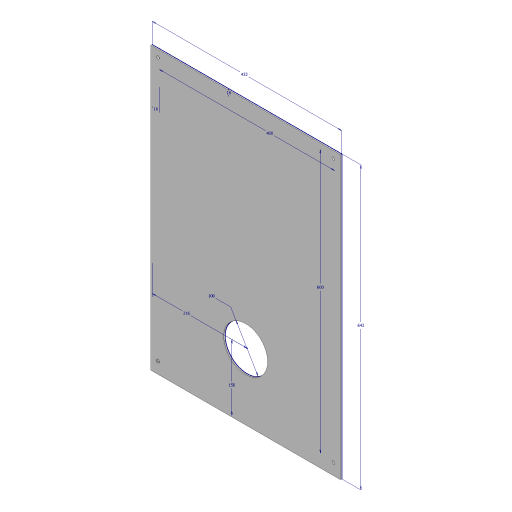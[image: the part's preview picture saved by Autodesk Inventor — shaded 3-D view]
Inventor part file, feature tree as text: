
AUTODESK INVENTOR PART (.ipt)
format: ipt  version: 2023 (Build 270158000, 158)  size: 101,376 bytes
history: native  units: mm
features: sketch x1, extrude x1, hole x1
ambient origin geometry x8: Origin, YZ Plane, XZ Plane, XY Plane, X Axis, Y Axis, Z Axis, Center Point
bodies: Solid1 (feature_tree)
feature tree (3):
  sketch  "Sketch1"  dims[d0=432.0mm d1=642.0mm d2=600.0mm d3=400.0mm d4=16.0mm d5=16.0mm d6=100.0mm d7=150.0mm d8=216.0mm d9=3.0mm d10=0.0mm d11=6.4mm d12=6.0mm d13=4.0mm d14=2.0mm d15=90.0deg d16=8.0mm d17=20.594885mm]
  extrude  "Extrusion1"  Depth=642.0mm
  hole  "Hole1"  [1 undecoded]
note: 1 required parameter value undecoded (feature->parameter linkage not recoverable at this tier; creation-order binding heuristic only, values carry confidence <= 0.55)
